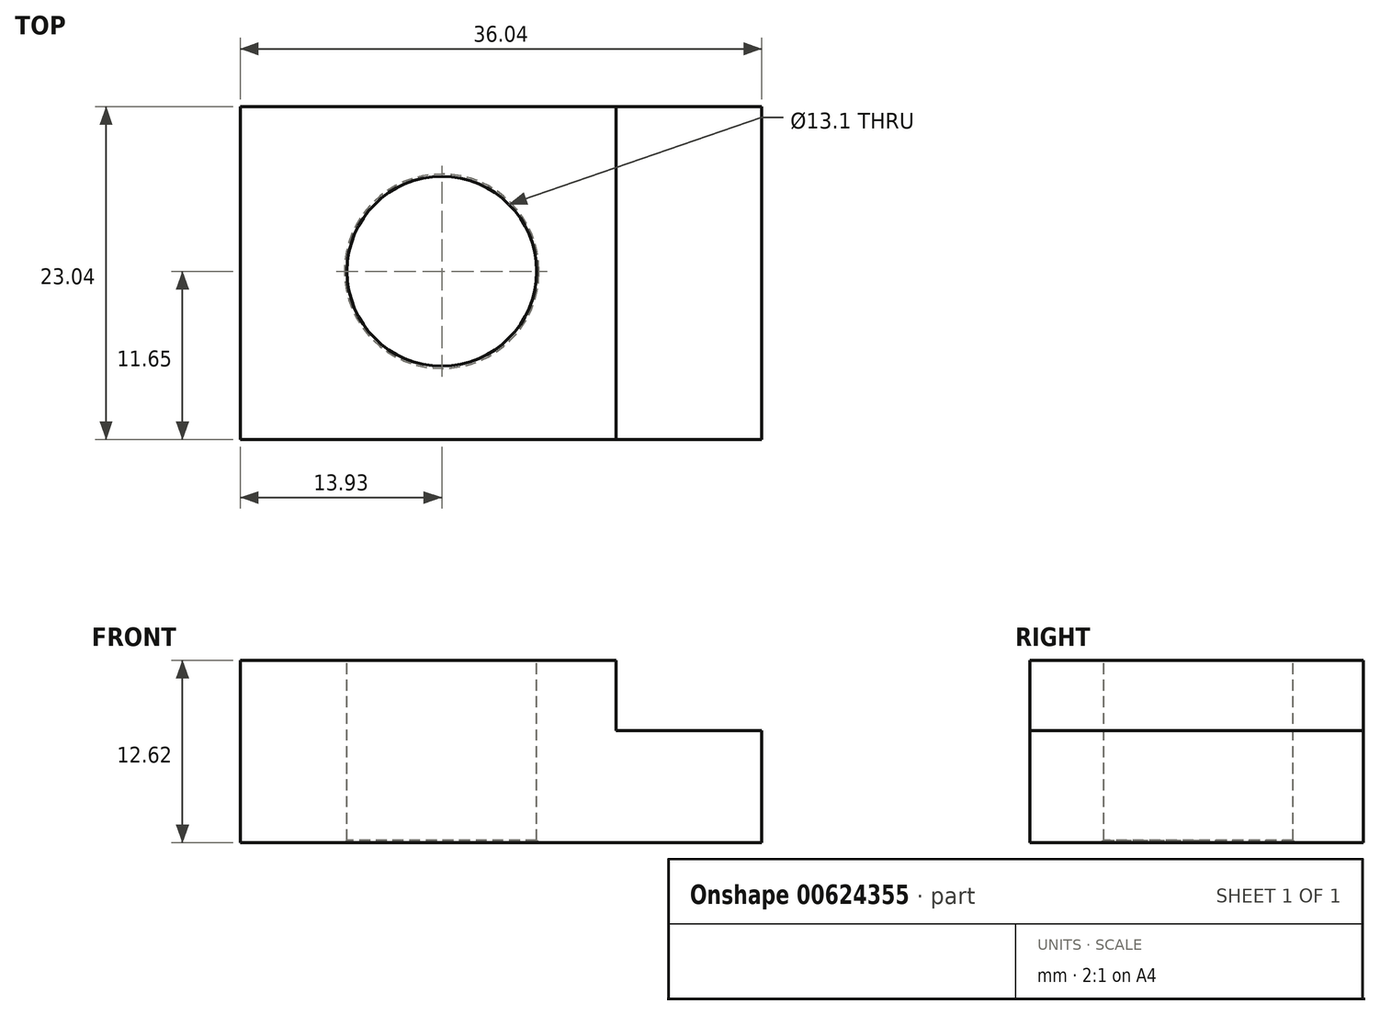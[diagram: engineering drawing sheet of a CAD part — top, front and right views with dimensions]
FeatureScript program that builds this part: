
annotation { "Feature Type Name" : "Feature", "Feature Type Description" : "" }
export const myFeature = defineFeature(function(context is Context, id is Id, definition is map)
    precondition{}
    {
        {
            var Q0;
            Q0=qCreatedBy(makeId("Top.planeOp"),FACE);
            var sketch = newSketch(context, id + "F0", { "sketchPlane" : qUnion([Q0])});
            skLineSegment(sketch, "E0.bottom", {"start": v(0, 0) * mm, "end": v(36.04, 0) * mm});
            skLineSegment(sketch, "E0.top", {"start": v(0, 23.04) * mm, "end": v(36.04, 23.04) * mm});
            skLineSegment(sketch, "E0.left", {"start": v(0, 0) * mm, "end": v(0, 23.04) * mm});
            skLineSegment(sketch, "E0.right", {"start": v(36.04, 0) * mm, "end": v(36.04, 23.04) * mm});
            skSolve(sketch);
        }
        {
            var Q0;
            Q0=makeQuery(id+"F0.imprint","IMPRINT",FACE,{"disambiguationData":[TD([[makeQuery(id+"F0.imprint","IMPRINT",EDGE,{"derivedFrom":sQuery(id+"F0.wireOp",EDGE,"E0.bottom")}),1.0]])]});
            extrude(context, id + "F1", {"entities" : qUnion([Q0]), "depth" : 7.74 * mm, "offsetDistance" : 25 * mm});
        }
        {
            var Q0;
            Q0=makeQuery(id+"F1.opExtrude","CAP_FACE",FACE,{"disambiguationData":[OSD([sQuery(id+"F0.wireOp",EDGE,"E0.bottom"),sQuery(id+"F0.wireOp",EDGE,"E0.top"),sQuery(id+"F0.wireOp",EDGE,"E0.left"),sQuery(id+"F0.wireOp",EDGE,"E0.right")])],"isStart":false});
            var sketch = newSketch(context, id + "F2", { "sketchPlane" : qUnion([Q0])});
            skLineSegment(sketch, "E1.bottom", {"start": v(0, 23.04) * mm, "end": v(25.98, 23.04) * mm});
            skLineSegment(sketch, "E1.top", {"start": v(0, 0) * mm, "end": v(25.98, 0) * mm});
            skLineSegment(sketch, "E1.left", {"start": v(0, 23.04) * mm, "end": v(0, 0) * mm});
            skLineSegment(sketch, "E1.right", {"start": v(25.98, 23.04) * mm, "end": v(25.98, 0) * mm});
            skSolve(sketch);
        }
        {
            var Q0;
            Q0=makeQuery(id+"F2.imprint","IMPRINT",FACE,{"disambiguationData":[TD([[makeQuery(id+"F2.imprint","IMPRINT",EDGE,{"derivedFrom":sQuery(id+"F2.wireOp",EDGE,"E1.bottom")}),-1.0]])]});
            extrude(context, id + "F3", {"entities" : qUnion([Q0]), "operationType" : NewBodyOperationType.ADD, "depth" : 4.88 * mm, "offsetDistance" : 25 * mm});
        }
        {
            var Q0;
            Q0=makeQuery(id+"F3.opExtrude","CAP_FACE",FACE,{"disambiguationData":[OSD([sQuery(id+"F2.wireOp",EDGE,"E1.bottom"),sQuery(id+"F2.wireOp",EDGE,"E1.top"),sQuery(id+"F2.wireOp",EDGE,"E1.left"),sQuery(id+"F2.wireOp",EDGE,"E1.right")])],"isStart":false});
            var sketch = newSketch(context, id + "F4", { "sketchPlane" : qUnion([Q0])});
            skCircle(sketch, "E2", {"center": v(13.93, 11.65) * mm, "radius": 6.55 * mm});
            skSolve(sketch);
        }
        {
            var Q0;
            Q0=makeQuery(id+"F4.imprint","IMPRINT",FACE,{"disambiguationData":[TD([[makeQuery(id+"F4.imprint","IMPRINT",EDGE,{"derivedFrom":sQuery(id+"F4.wireOp",EDGE,"E2")}),1.0]])]});
            extrude(context, id + "F5", {"entities" : qUnion([Q0]), "operationType" : NewBodyOperationType.REMOVE, "endBound" : BoundingType.THROUGH_ALL, "oppositeDirection" : true, "depth" : 25 * mm, "offsetDistance" : 25 * mm});
        }
        {
            var Q0;
            Q0=makeQuery(id+"F5.boolean.opBoolean","COPY",EDGE,{"derivedFrom":makeQuery(id+"F5.opExtrude","CAP_EDGE",EDGE,{"disambiguationData":[OSD([sQuery(id+"F4.wireOp",EDGE,"E2")])],"isStart":true})});
            var Q1;
            Q1=makeQuery(id+"F5.boolean.opBoolean","INTERSECT",EDGE,{"derivedFrom":[makeQuery(id+"F1.opExtrude","CAP_FACE",FACE,{"disambiguationData":[OSD([sQuery(id+"F0.wireOp",EDGE,"E0.bottom"),sQuery(id+"F0.wireOp",EDGE,"E0.top"),sQuery(id+"F0.wireOp",EDGE,"E0.left"),sQuery(id+"F0.wireOp",EDGE,"E0.right")])],"isStart":true}),makeQuery(id+"F5.opExtrude","SWEPT_FACE",FACE,{"disambiguationData":[OSD([sQuery(id+"F4.wireOp",EDGE,"E2")])]})]});
            chamfer(context, id + "F6", {"entities" : qUnion([Q0, Q1]), "chamferType" : ChamferType.OFFSET_ANGLE, "width" : 0.18 * mm, "oppositeDirection" : false, "angle" : 45 * degree, "tangentPropagation" : true});
        }
    });
